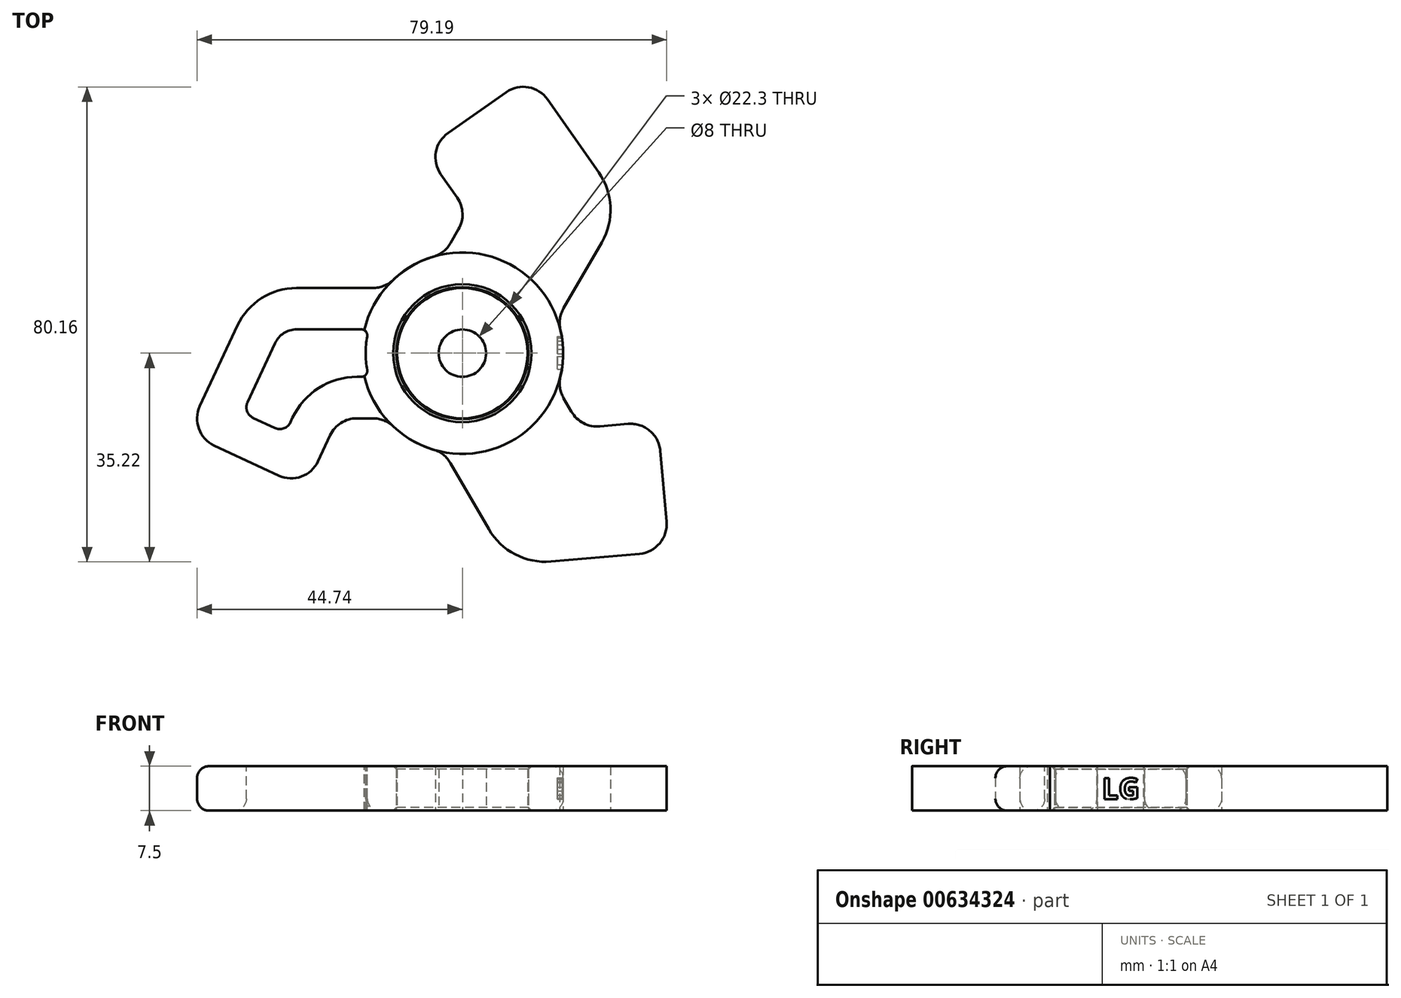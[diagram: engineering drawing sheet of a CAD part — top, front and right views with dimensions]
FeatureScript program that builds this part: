
annotation { "Feature Type Name" : "Feature", "Feature Type Description" : "" }
export const myFeature = defineFeature(function(context is Context, id is Id, definition is map)
    precondition{}
    {
        {
            var Q0;
            Q0=qCreatedBy(makeId("Top.planeOp"),FACE);
            var sketch = newSketch(context, id + "F0", { "sketchPlane" : qUnion([Q0])});
            skCircle(sketch, "E0", {"center": v(0, 0) * mm, "radius": 11 * mm});
            skCircle(sketch, "E1", {"center": v(0, 0) * mm, "radius": 4 * mm});
            skSolve(sketch);
        }
        {
            var Q0;
            Q0=makeQuery(id+"F0.imprint","IMPRINT",FACE,{"disambiguationData":[TD([[makeQuery(id+"F0.imprint","IMPRINT",EDGE,{"derivedFrom":sQuery(id+"F0.wireOp",EDGE,"E0")}),1.0]])]});
            extrude(context, id + "F1", {"entities" : qUnion([Q0]), "depth" : 7 * mm, "offsetDistance" : 25 * mm});
        }
        {
            var Q0;
            Q0=qCreatedBy(makeId("Top.planeOp"),FACE);
            var sketch = newSketch(context, id + "F2", { "sketchPlane" : qUnion([Q0])});
            skLineSegment(sketch, "E2.bottom", {"start": v(-27.96, 11) * mm, "end": v(-15.1, 11) * mm});
            skLineSegment(sketch, "E2.top", {"start": v(-17.77, -11) * mm, "end": v(-15.1, -11) * mm});
            skPoint(sketch, "E2.middle", {"position": v(0, 0) * mm});
            skArc(sketch, "E3.0", {"start": v(-11.67, -12.36) * mm, "mid": v(17, 0) * mm, "end": v(-11.67, 12.36) * mm});
            skPoint(sketch, "E2.right.start.orphan", {"position": v(27.96, 11) * mm});
            skPoint(sketch, "E4.orphan", {"position": v(27.96, -11) * mm});
            skArc(sketch, "E5", {"start": v(-27.96, 11) * mm, "mid": v(-33.87, 9.28) * mm, "end": v(-37.93, 4.65) * mm});
            skLineSegment(sketch, "E6.bottom", {"start": v(-41.85, -15.6) * mm, "end": v(-30.98, -20.66) * mm});
            skLineSegment(sketch, "E6.left", {"start": v(-44.27, -8.95) * mm, "end": v(-37.93, 4.65) * mm});
            skLineSegment(sketch, "E6.right", {"start": v(-24.33, -18.24) * mm, "end": v(-22.3, -13.89) * mm});
            skPoint(sketch, "E7.orphan", {"position": v(-27.96, -11) * mm});
            skPoint(sketch, "E8.visualSharp", {"position": v(-46.38, -13.48) * mm});
            skArc(sketch, "E8.filletArc", {"start": v(-44.27, -8.95) * mm, "mid": v(-44.44, -12.77) * mm, "end": v(-41.85, -15.6) * mm});
            skPoint(sketch, "E9.visualSharp", {"position": v(-26.44, -22.77) * mm});
            skArc(sketch, "E9.filletArc", {"start": v(-30.98, -20.66) * mm, "mid": v(-27.15, -20.83) * mm, "end": v(-24.33, -18.24) * mm});
            skPoint(sketch, "E10.visualSharp", {"position": v(-20.95, -11) * mm});
            skArc(sketch, "E10.filletArc", {"start": v(-17.77, -11) * mm, "mid": v(-20.45, -11.78) * mm, "end": v(-22.3, -13.89) * mm});
            skPoint(sketch, "E11.visualSharp", {"position": v(-12.96, -11) * mm});
            skArc(sketch, "E11.filletArc", {"start": v(-11.67, -12.36) * mm, "mid": v(-13.25, -11.35) * mm, "end": v(-15.1, -11) * mm});
            skPoint(sketch, "E12.visualSharp", {"position": v(-12.96, 11) * mm});
            skArc(sketch, "E12.filletArc", {"start": v(-15.1, 11) * mm, "mid": v(-13.25, 11.35) * mm, "end": v(-11.67, 12.36) * mm});
            skCircle(sketch, "E13.0", {"center": v(0, 0) * mm, "radius": 11.15 * mm});
            skSolve(sketch);
        }
        {
            var Q0;
            Q0=makeQuery(id+"F2.imprint","IMPRINT",FACE,{"disambiguationData":[TD([[makeQuery(id+"F2.imprint","IMPRINT",EDGE,{"derivedFrom":sQuery(id+"F2.wireOp",EDGE,"E2.bottom")}),-1.0]])]});
            extrude(context, id + "F3", {"entities" : qUnion([Q0]), "depth" : 7.5 * mm, "offsetDistance" : 25 * mm});
        }
        {
            var Q0;
            Q0=makeQuery(id+"F3.opExtrude","SWEPT_BODY",BODY,{"disambiguationData":[OSD([sQuery(id+"F2.wireOp",EDGE,"E2.bottom"),sQuery(id+"F2.wireOp",EDGE,"E2.top"),sQuery(id+"F2.wireOp",EDGE,"E3.0"),sQuery(id+"F2.wireOp",EDGE,"E5"),sQuery(id+"F2.wireOp",EDGE,"E6.bottom"),sQuery(id+"F2.wireOp",EDGE,"E6.left"),sQuery(id+"F2.wireOp",EDGE,"E6.right"),sQuery(id+"F2.wireOp",EDGE,"E8.filletArc"),sQuery(id+"F2.wireOp",EDGE,"E9.filletArc"),sQuery(id+"F2.wireOp",EDGE,"E10.filletArc"),sQuery(id+"F2.wireOp",EDGE,"E11.filletArc"),sQuery(id+"F2.wireOp",EDGE,"E12.filletArc"),sQuery(id+"F2.wireOp",EDGE,"E13.0")])]});
            var Q1;
            Q1=makeQuery(id+"F3.opExtrude","CAP_EDGE",EDGE,{"disambiguationData":[OSD([sQuery(id+"F2.wireOp",EDGE,"E13.0")])],"isStart":false});
            circularPattern(context, id + "F4", {"operationType" : NewBodyOperationType.ADD, "entities" : qUnion([Q0]), "axis" : qUnion([Q1]), "angle" : 360 * degree, "instanceCount" : 3, "equalSpace" : true});
        }
        {
            var Q0;
            Q0=makeQuery(id+"F3.opExtrude","CAP_FACE",FACE,{"disambiguationData":[OSD([sQuery(id+"F2.wireOp",EDGE,"E2.bottom"),sQuery(id+"F2.wireOp",EDGE,"E2.top"),sQuery(id+"F2.wireOp",EDGE,"E3.0"),sQuery(id+"F2.wireOp",EDGE,"E5"),sQuery(id+"F2.wireOp",EDGE,"E6.bottom"),sQuery(id+"F2.wireOp",EDGE,"E6.left"),sQuery(id+"F2.wireOp",EDGE,"E6.right"),sQuery(id+"F2.wireOp",EDGE,"E8.filletArc"),sQuery(id+"F2.wireOp",EDGE,"E9.filletArc"),sQuery(id+"F2.wireOp",EDGE,"E10.filletArc"),sQuery(id+"F2.wireOp",EDGE,"E11.filletArc"),sQuery(id+"F2.wireOp",EDGE,"E12.filletArc"),sQuery(id+"F2.wireOp",EDGE,"E13.0")])],"isStart":false});
            var sketch = newSketch(context, id + "F5", { "sketchPlane" : qUnion([Q0])});
            skLineSegment(sketch, "E14.0", {"start": v(-27.96, 4) * mm, "end": v(-17.04, 4) * mm});
            skArc(sketch, "E14.1", {"start": v(-27.96, 4) * mm, "mid": v(-30.11, 3.37) * mm, "end": v(-31.59, 1.7) * mm});
            skLineSegment(sketch, "E14.2", {"start": v(-36.24, -8.28) * mm, "end": v(-31.59, 1.7) * mm});
            skLineSegment(sketch, "E14.3", {"start": v(-17.77, -4) * mm, "end": v(-17.04, -4) * mm});
            skArc(sketch, "E14.4", {"start": v(-17.77, -4) * mm, "mid": v(-24.22, -5.88) * mm, "end": v(-28.64, -10.93) * mm});
            skLineSegment(sketch, "E14.5", {"start": v(-28.99, -11.66) * mm, "end": v(-28.64, -10.93) * mm});
            skLineSegment(sketch, "E14.6", {"start": v(-35.27, -10.94) * mm, "end": v(-31.64, -12.63) * mm});
            skPoint(sketch, "E15.visualSharp", {"position": v(-37.08, -10.1) * mm});
            skArc(sketch, "E15.filletArc", {"start": v(-36.24, -8.28) * mm, "mid": v(-36.3, -9.8) * mm, "end": v(-35.27, -10.94) * mm});
            skPoint(sketch, "E16.visualSharp", {"position": v(-29.83, -13.47) * mm});
            skArc(sketch, "E16.filletArc", {"start": v(-31.64, -12.63) * mm, "mid": v(-30.11, -12.7) * mm, "end": v(-28.99, -11.66) * mm});
            skArc(sketch, "E17.0", {"start": v(-16.05, 2.83) * mm, "mid": v(-16.3, 0) * mm, "end": v(-16.05, -2.83) * mm});
            skPoint(sketch, "E18.visualSharp", {"position": v(-15.8, 4) * mm});
            skArc(sketch, "E18.filletArc", {"start": v(-16.05, 2.83) * mm, "mid": v(-16.27, 3.64) * mm, "end": v(-17.04, 4) * mm});
            skPoint(sketch, "E19.visualSharp", {"position": v(-15.8, -4) * mm});
            skArc(sketch, "E19.filletArc", {"start": v(-17.04, -4) * mm, "mid": v(-16.27, -3.64) * mm, "end": v(-16.05, -2.83) * mm});
            skSolve(sketch);
        }
        {
            var Q0;
            Q0=makeQuery(id+"F5.imprint","IMPRINT",FACE,{"disambiguationData":[TD([[makeQuery(id+"F5.imprint","IMPRINT",EDGE,{"derivedFrom":sQuery(id+"F5.wireOp",EDGE,"E14.0")}),-1.0]])]});
            extrude(context, id + "F6", {"entities" : qUnion([Q0]), "operationType" : NewBodyOperationType.REMOVE, "oppositeDirection" : true, "depth" : 25 * mm, "offsetDistance" : 25 * mm});
        }
        {
            var Q0;
            Q0=makeQuery(id+"F6.boolean.opBoolean","COPY",EDGE,{"derivedFrom":makeQuery(id+"F6.opExtrude","CAP_EDGE",EDGE,{"disambiguationData":[OSD([sQuery(id+"F5.wireOp",EDGE,"E14.0")])],"isStart":true})});
            var Q1;
            {var subQ0=makeQuery(id+"F3.opExtrude","CAP_FACE",FACE,{"disambiguationData":[OSD([sQuery(id+"F2.wireOp",EDGE,"E2.bottom"),sQuery(id+"F2.wireOp",EDGE,"E2.top"),sQuery(id+"F2.wireOp",EDGE,"E3.0"),sQuery(id+"F2.wireOp",EDGE,"E5"),sQuery(id+"F2.wireOp",EDGE,"E6.bottom"),sQuery(id+"F2.wireOp",EDGE,"E6.left"),sQuery(id+"F2.wireOp",EDGE,"E6.right"),sQuery(id+"F2.wireOp",EDGE,"E8.filletArc"),sQuery(id+"F2.wireOp",EDGE,"E9.filletArc"),sQuery(id+"F2.wireOp",EDGE,"E10.filletArc"),sQuery(id+"F2.wireOp",EDGE,"E11.filletArc"),sQuery(id+"F2.wireOp",EDGE,"E12.filletArc"),sQuery(id+"F2.wireOp",EDGE,"E13.0")])],"isStart":true});Q1=makeQuery(id+"F6.boolean.opBoolean","INTERSECT",EDGE,{"derivedFrom":[makeQuery(id+"F4.boolean.opBoolean","MERGE",FACE,{"derivedFrom":[subQ0,makeQuery(id+"F4.opPattern","COPY",FACE,{"derivedFrom":subQ0,"instanceName":"1"})]}),makeQuery(id+"F6.opExtrude","SWEPT_FACE",FACE,{"disambiguationData":[OSD([sQuery(id+"F5.wireOp",EDGE,"E14.6")])]})]});}
            fillet(context, id + "F7", {"entities" : qUnion([Q0, Q1]), "radius" : 2 * mm, "tangentPropagation" : true, "allowEdgeOverflow" : false});
        }
        {
            var Q0;
            {var subQ0=sQuery(id+"F2.wireOp",EDGE,"E12.filletArc");var subQ2=sQuery(id+"F2.wireOp",EDGE,"E3.0");Q0=makeQuery(id+"F4.boolean.opBoolean","SPLIT",EDGE,{"disambiguationData":[TD([makeQuery(id+"F3.opExtrude","SWEPT_FACE",FACE,{"disambiguationData":[OSD([subQ0])]})])],"derivedFrom":makeQuery(id+"F3.opExtrude","CAP_EDGE",EDGE,{"disambiguationData":[OSD([subQ2])],"isStart":true})});}
            var Q1;
            {var subQ0=sQuery(id+"F2.wireOp",EDGE,"E12.filletArc");var subQ2=sQuery(id+"F2.wireOp",EDGE,"E3.0");Q1=makeQuery(id+"F4.boolean.opBoolean","SPLIT",EDGE,{"disambiguationData":[TD([makeQuery(id+"F3.opExtrude","SWEPT_FACE",FACE,{"disambiguationData":[OSD([subQ0])]})])],"derivedFrom":makeQuery(id+"F3.opExtrude","CAP_EDGE",EDGE,{"disambiguationData":[OSD([subQ2])],"isStart":false})});}
            fillet(context, id + "F8", {"entities" : qUnion([Q0, Q1]), "radius" : 2 * mm, "tangentPropagation" : true, "allowEdgeOverflow" : false});
        }
        {
            var Q0;
            Q0=makeQuery(id+"F3.opExtrude","CAP_EDGE",EDGE,{"disambiguationData":[OSD([sQuery(id+"F2.wireOp",EDGE,"E13.0")])],"isStart":true});
            var Q1;
            Q1=makeQuery(id+"F3.opExtrude","CAP_EDGE",EDGE,{"disambiguationData":[OSD([sQuery(id+"F2.wireOp",EDGE,"E13.0")])],"isStart":false});
            chamfer(context, id + "F9", {"entities" : qUnion([Q0, Q1]), "width" : .5 * mm, "tangentPropagation" : true});
        }
        {
            var Q0;
            Q0=qCreatedBy(makeId("Right.planeOp"),FACE);
            cPlane(context, id + "F10", {"entities" : qUnion([Q0]), "cplaneType" : CPlaneType.OFFSET, "offset" : 25 * mm, "width" : 150 * mm, "height" : 150 * mm});
        }
        {
            var Q0;
            Q0=qCreatedBy(id+"F10.planeOp",FACE);
            var sketch = newSketch(context, id + "F11", { "sketchPlane" : qUnion([Q0])});
            skText(sketch, "E20", { "text": "LG", "fontName": "OpenSans-Bold.ttf"});
            const initialGuessF11  = {"E20": [-0.00317, 0.00196, 1, 0, 0.00356]};
            skSetInitialGuess(sketch, initialGuessF11);
            skSolve(sketch);
        }
        {
            var Q0;
            Q0=qSketchRegion(id+"F11",true);
            extrude(context, id + "F12", {"entities" : qUnion([Q0]), "operationType" : NewBodyOperationType.REMOVE, "oppositeDirection" : true, "depth" : 9 * mm, "offsetDistance" : 25 * mm});
        }
    });
